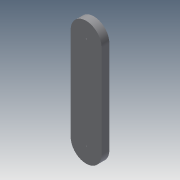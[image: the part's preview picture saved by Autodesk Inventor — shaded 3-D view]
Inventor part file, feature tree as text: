
AUTODESK INVENTOR PART (.ipt)
format: ipt  version: 2013 (Build 170138000, 138)  size: 99,840 bytes
history: native  units: mm
features: sketch x7, extrude x3
ambient origin geometry x8: Origin, YZ Plane, XZ Plane, XY Plane, X Axis, Y Axis, Z Axis, Center Point
bodies: Solid1 (feature_tree)
feature tree (10):
  extrude  "Extrusion1"  Depth=18.0mm
  extrude  "Extrusion2"  Depth=1.5mm TaperAngle=0.0deg
  sketch  "Sketch3"  dims[d5=3.0mm d6=3.0mm]
  sketch  "Sketch4"  dims[d7=2.0mm d8=0.0mm]
  sketch  "Sketch5"  dims[d13=0.2mm]
  sketch  "Sketch6"  dims[d14=0.2mm]
  extrude  "Extrusion3"  Depth=3.0mm
  sketch  "Sketch1"  dims[d0=6.0mm d1=18.0mm]
  sketch  "Sketch2"  dims[d2=6.0mm d3=1.5mm d4=0.0mm]
  sketch  "Sketch7"  dims[d15=1.5mm d16=0.0mm]
